# Revit family: Shower-Showerhead-KOHLER-Awaken-K-72423_1
name_source: partatom
category: Plumbing Fixtures
units: mm (PartAtom-declared; Revit-internal decimal feet)

## family parameters
Cut with Voids When Loaded = No
Host = Face
Maintain Annotation Orientation = No
OmniClass Number = 23.31.17.00
OmniClass Title = Showers
Part Type = Normal
Room Calculation Point = No
Round Connector Dimension = Use Diameter
Shared = No

## types (5) — shared parameters
ADA Compliant = No
Assembly Code = D2010700
CW Connection = No
Cold Water Inlet = Cold Water Inlet
Date Modified = 05/20/2022
Default Elevation = 42"
Description = single-function showerhead
Drain Included = No
HW Connection = Yes
Height = 3 3/4"
Hot Water Inlet = Hot Water Inlet
Length = 2 5/8"
Manufacturer = Kohler Co.
Master Format 2014 = 22 42 23
Master Format 2014 Name = Residential Showers
Material = Plastic
Pressure = 0.00 psi
Product Documentation Link = https://www.us.kohler.com
Product Name = Awaken
Product Page URL = http://www.us.kohler.com
Tempered Water Inlet = Tempered Water Inlet
URL = https://www.us.kohler.com
Vent Connection = No
Waste Connection = No
Waste Water Outlet = Waste Water Outlet
Width = 3 3/4"

## per-type parameters (varying)
| type | Finish | Flow Rate | Model | Type | WaterSense Certified |
| 1.75 GPM, 0-White | Kohler-Plastic-0-White | 2 GPM | K-72423-0 | 1 | Yes |
| 1.75 GPM, CP-Polished Chrome | KOHLER-Plastic-CP-Polished_Chrome | 2 GPM | K-72423-CP | 2 | Yes |
| 1.75 GPM, BN-Vibrant Brushed Nickel | KOHLER-Plastic-BN-Vibrant_Brushed_Nickel | 2 GPM | K-72423-BN | 3 | Yes |
| 2.5 GPM, CP-Polished Chrome | KOHLER-Plastic-CP-Polished_Chrome | 3 GPM | K-72423-Y-CP | 4 | No |
| 2.5 GPM, BN-Vibrant Brushed Nickel | KOHLER-Plastic-BN-Vibrant_Brushed_Nickel | 3 GPM | K-72423-Y-BN | 5 | No |

## geometry (parser evidence)
native form markers: Sweep x3
no freeform markers — native parametric forms only
